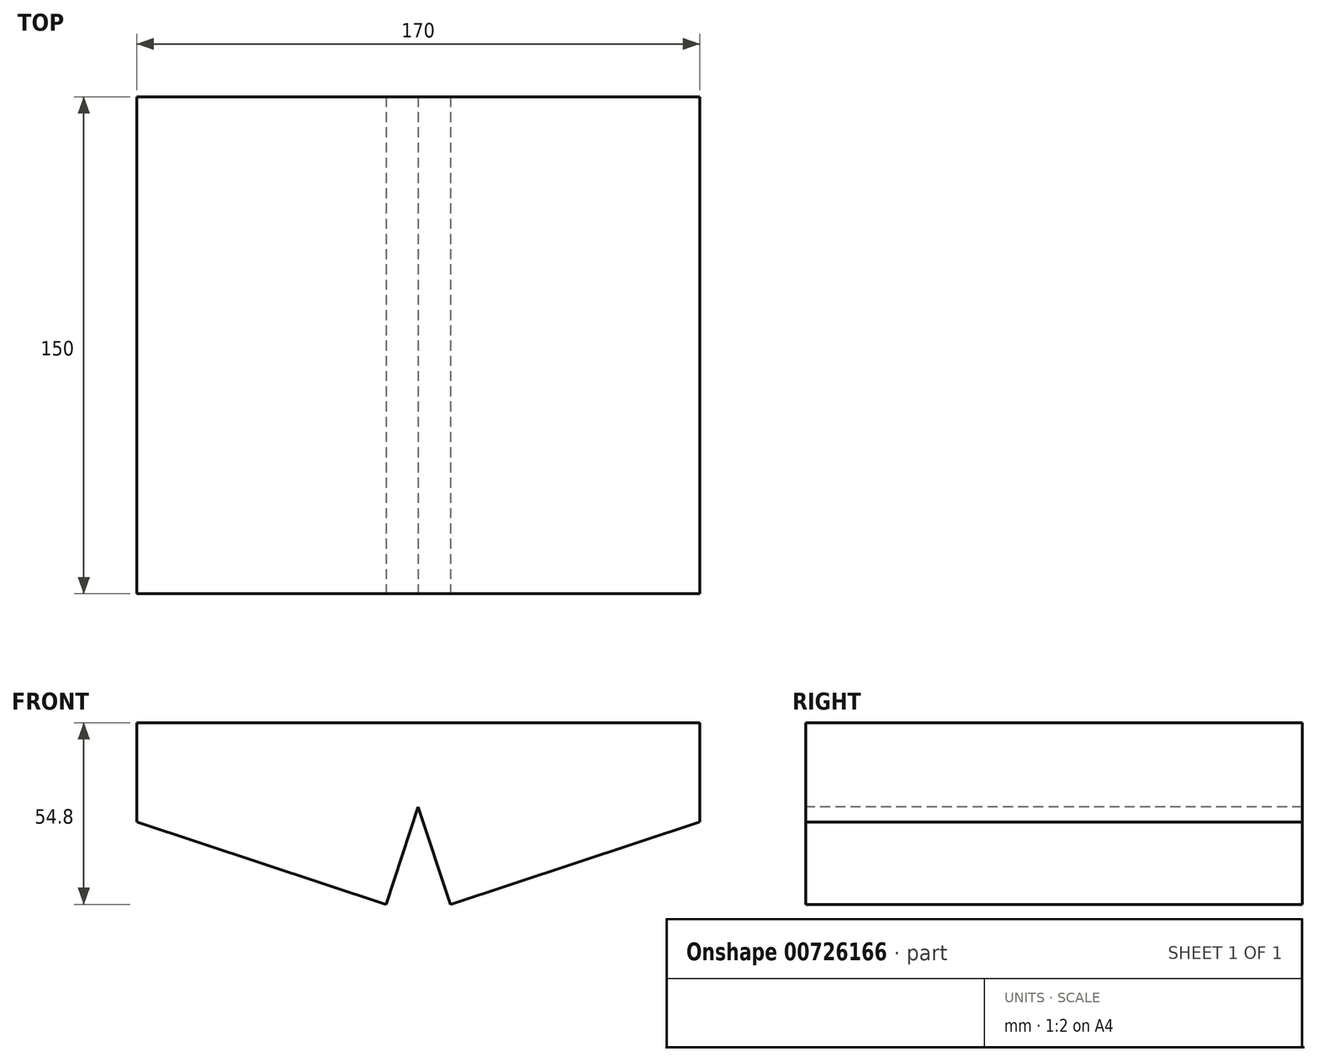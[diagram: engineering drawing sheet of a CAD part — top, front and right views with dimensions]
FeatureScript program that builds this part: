
annotation { "Feature Type Name" : "Feature", "Feature Type Description" : "" }
export const myFeature = defineFeature(function(context is Context, id is Id, definition is map)
    precondition{}
    {
        {
            var Q0;
            Q0=qCreatedBy(makeId("Front.planeOp"),FACE);
            var sketch = newSketch(context, id + "F0", { "sketchPlane" : qUnion([Q0])});
            skLineSegment(sketch, "E0.top", {"start": v(-20.04, 65.04) * mm, "end": v(-105.04, 65.04) * mm});
            skLineSegment(sketch, "E1", {"start": v(-29.74, 10.24) * mm, "end": v(-20.04, 39.64) * mm});
            skLineSegment(sketch, "E2", {"start": v(-29.74, 10.24) * mm, "end": v(-104.94, 35.04) * mm});
            skLineSegment(sketch, "E3", {"start": v(-105.04, 65.04) * mm, "end": v(-105.04, 35.04) * mm});
            skLineSegment(sketch, "E4.MirrorCS", {"start": v(64.96, 65.04) * mm, "end": v(64.96, 35.04) * mm});
            skLineSegment(sketch, "E5.MirrorCS", {"start": v(-10.34, 10.24) * mm, "end": v(64.86, 35.04) * mm});
            skLineSegment(sketch, "E6.MirrorCS", {"start": v(-20.04, 65.04) * mm, "end": v(64.96, 65.04) * mm});
            skLineSegment(sketch, "E7.MirrorCS", {"start": v(-10.34, 10.24) * mm, "end": v(-20.04, 39.64) * mm});
            skSolve(sketch);
        }
        {
            var Q0;
            Q0=sQuery(id+"F0.wireOp",EDGE,"E0.top");
            var Q1;
            Q1=sQuery(id+"F0.wireOp",EDGE,"E7.MirrorCS");
            var Q2;
            Q2=sQuery(id+"F0.wireOp",EDGE,"E4.MirrorCS");
            var Q3;
            Q3=sQuery(id+"F0.wireOp",EDGE,"E2");
            var Q4;
            Q4=sQuery(id+"F0.wireOp",EDGE,"E6.MirrorCS");
            var Q5;
            Q5=sQuery(id+"F0.wireOp",EDGE,"E3");
            var Q6;
            Q6=sQuery(id+"F0.wireOp",EDGE,"E1");
            var Q7;
            Q7=sQuery(id+"F0.wireOp",EDGE,"E5.MirrorCS");
            extrude(context, id + "F1", {"bodyType" : ToolBodyType.SURFACE, "surfaceEntities" : qUnion([Q0, Q1, Q2, Q3, Q4, Q5, Q6, Q7]), "depth" : 150 * mm, "offsetDistance" : 25 * mm});
        }
    });
